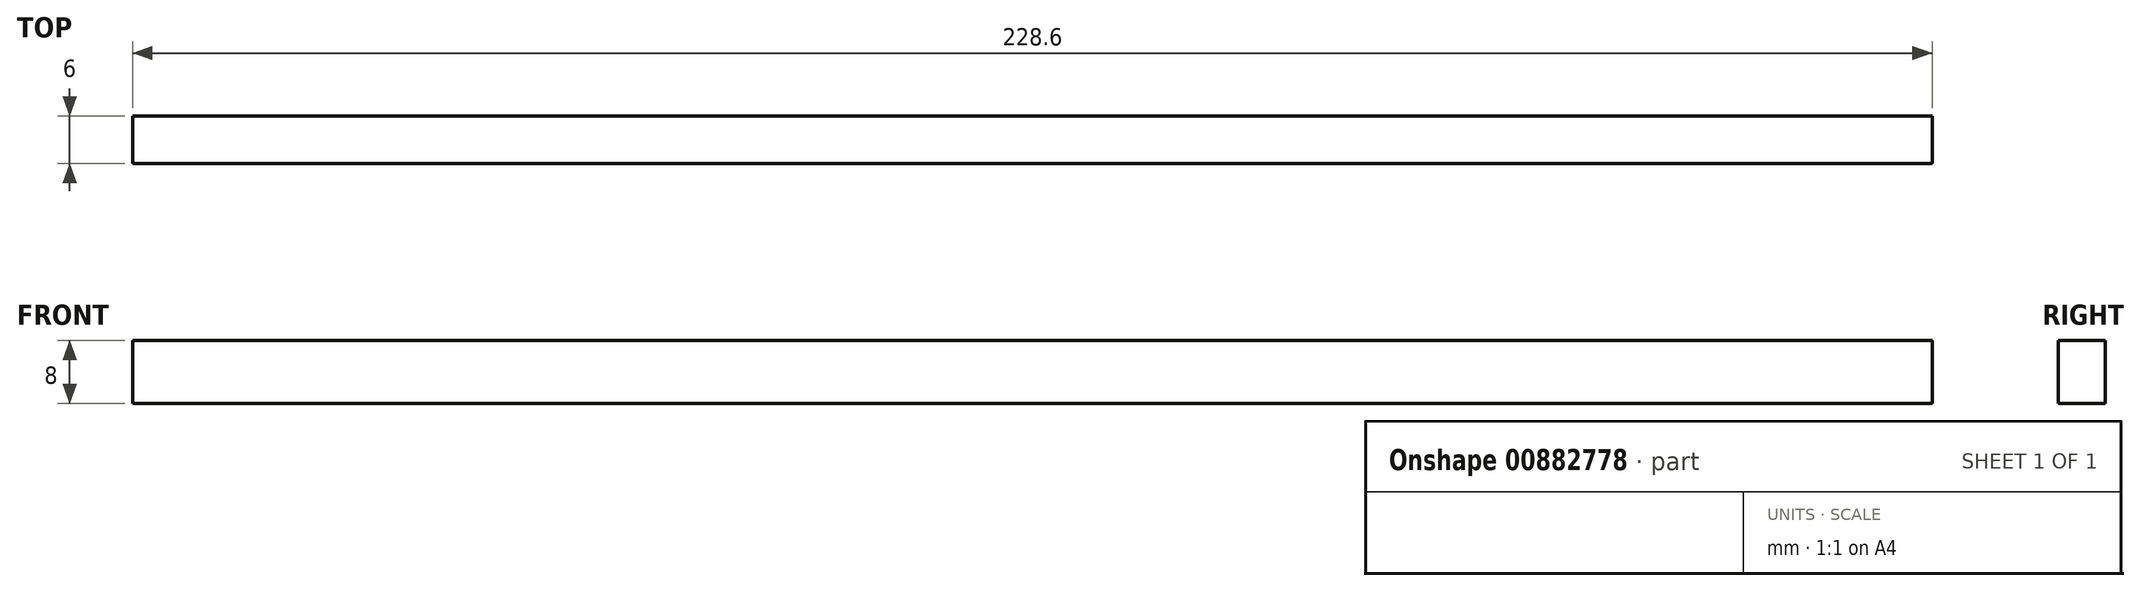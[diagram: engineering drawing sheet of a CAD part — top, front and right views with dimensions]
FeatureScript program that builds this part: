
annotation { "Feature Type Name" : "Feature", "Feature Type Description" : "" }
export const myFeature = defineFeature(function(context is Context, id is Id, definition is map)
    precondition{}
    {
        {
            var Q0;
            Q0=qCreatedBy(makeId("Front.planeOp"),FACE);
            var sketch = newSketch(context, id + "F0", { "sketchPlane" : qUnion([Q0])});
            skLineSegment(sketch, "E0.bottom", {"start": v(114.3, -4) * mm, "end": v(-114.3, -4) * mm});
            skLineSegment(sketch, "E0.top", {"start": v(114.3, 4) * mm, "end": v(-114.3, 4) * mm});
            skLineSegment(sketch, "E0.left", {"start": v(114.3, -4) * mm, "end": v(114.3, 4) * mm});
            skLineSegment(sketch, "E0.right", {"start": v(-114.3, -4) * mm, "end": v(-114.3, 4) * mm});
            skPoint(sketch, "E0.middle", {"position": v(0, 0) * mm});
            skSolve(sketch);
        }
        {
            var Q0;
            Q0 = qSketchRegion(id + "F0", true);
            extrude(context, id + "F1", {"entities" : qUnion([Q0]), "depth" : 6 * mm, "offsetDistance" : 25.4 * mm});
        }
    });
